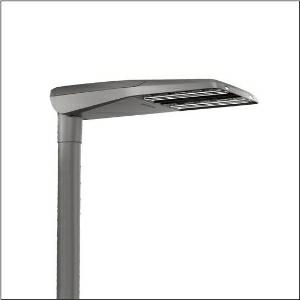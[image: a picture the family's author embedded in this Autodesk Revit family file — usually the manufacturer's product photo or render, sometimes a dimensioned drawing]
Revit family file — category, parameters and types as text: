
# Revit family: streetlight_sl_11_iq_midi___st1_2p1_0_5xc3g51f08me_c537
name_source: partatom
category: Lighting Fixtures
units: mm (PartAtom-declared; Revit-internal decimal feet)

## family parameters
Cut with Voids When Loaded = No
Host = Face
Light Source = No
Part Type = Normal
Room Calculation Point = No
Round Connector Dimension = Use Diameter
Shared = No

## types (1)
- --- (1 x LED, 17750 lm, 124.7 W, 3000K)
    Apparent Load = 125 VA
    CIE Flux Codes = 31 68 95 100 100
    Color Rendering = 70
    Color Temperature = 3000K
    Default Elevation = 1800 mm
    Description = Streetlight SL 11 iQ midi, mast luminaire, primary light control with 3 zone facetted reflector, of plastic, silver coated, highly specular, primary optical cover: cover, of PMMA, transparent, light distribution: ST1.2P1.0, light emission: direct distribution, primary light characteristic: asymmetric, installation type: post-top, side-entry, LED, High Power LED, rated luminous flux: 17.750lm, luminous efficacy: 142lm/W, light colour: 730, colour temperature: 3000K, control: Street-Remote, optimised constant luminous flux control (CLO 2.0), Auto-Match, Desk-Remote (wireless, voltage-free reading and setting of iQ features in the workshop via application-optimized NFC function/RFID function), Light-Fading, Smart-Wire, Night-Set, Lumen-Switch, Temp-Guard, with cable H07RN-F 5x 1.5mm², mains connection: 220..240V, AC, 50/60Hz, connection cable pre-assembled, cable length: 12,5m, start of lifetime: 125W, end of lifetime: 132W, reduction: 57W, luminaire housing, of diecast aluminium, powder-coated, Siteco® metallic grey (DB 702S), length: 780mm, width: 376mm, height: 118mm, spigot size: 60/76mm (post-top) and 42/60/76mm (side-entry), mast flange for spigot size: 42mm: 5XC10008XM4, 60mm: 5XC10008XM2, 76/60mm: 5XC10108XM1, equipment: Power, protection rating (complete): IP66, insulation class (complete): insulation class II (safety insulation), certification: CE, ENEC, VDE, impact resistance: IK09, permissible operating ambient temperature for outdoor applications: -25..+50°C, standard-compliant lighting for roads and squares, packaging unit: 1 piece

Light Distribution: ST1.2P1.0
    Height = 118 mm
    Lamp = 1 x LED
    Lamp Light Flux = 17750 lm
    Lamp Power = 124.7 W
    Lamp count = 1
    Length = 780 mm
    Luminous efficacy = 142 lm/W
    Manufacturer = Siteco
    ModVariant = No
    Model = 5XC3G51F08ME
    Number of Poles = 1
    OnlyDefault = Yes
    Power Factor = 1
    Product Name = Streetlight SL 11 iQ midi | ST1.2P1.0
    Product group = mast luminaire | pylon top
    ProductGroupID = 6100
    Protection Class = Protection class II
    Protection Degree = IP 66
    RLX_Detail_Level = 1
    RlxData = <blob elided: 70285 chars, md5=30fe430c>
    Socket = socket
    Standby Power = 0 W
    System Light Flux = 17750 lm
    System Power = 125 W
    Type Comments = factory setting: luminous flux: 100 % | dim-lin: 254 | 557 mA
    Type Image = l_1005960.jpg
    URL = http://relux.com
    VarID = @adj_116133
    Voltage = 0 V
    Weight = 0.00 kg
    Width = 376 mm

## geometry (parser evidence)
native form markers: Blend x4, Sweep x10
no freeform markers — native parametric forms only
